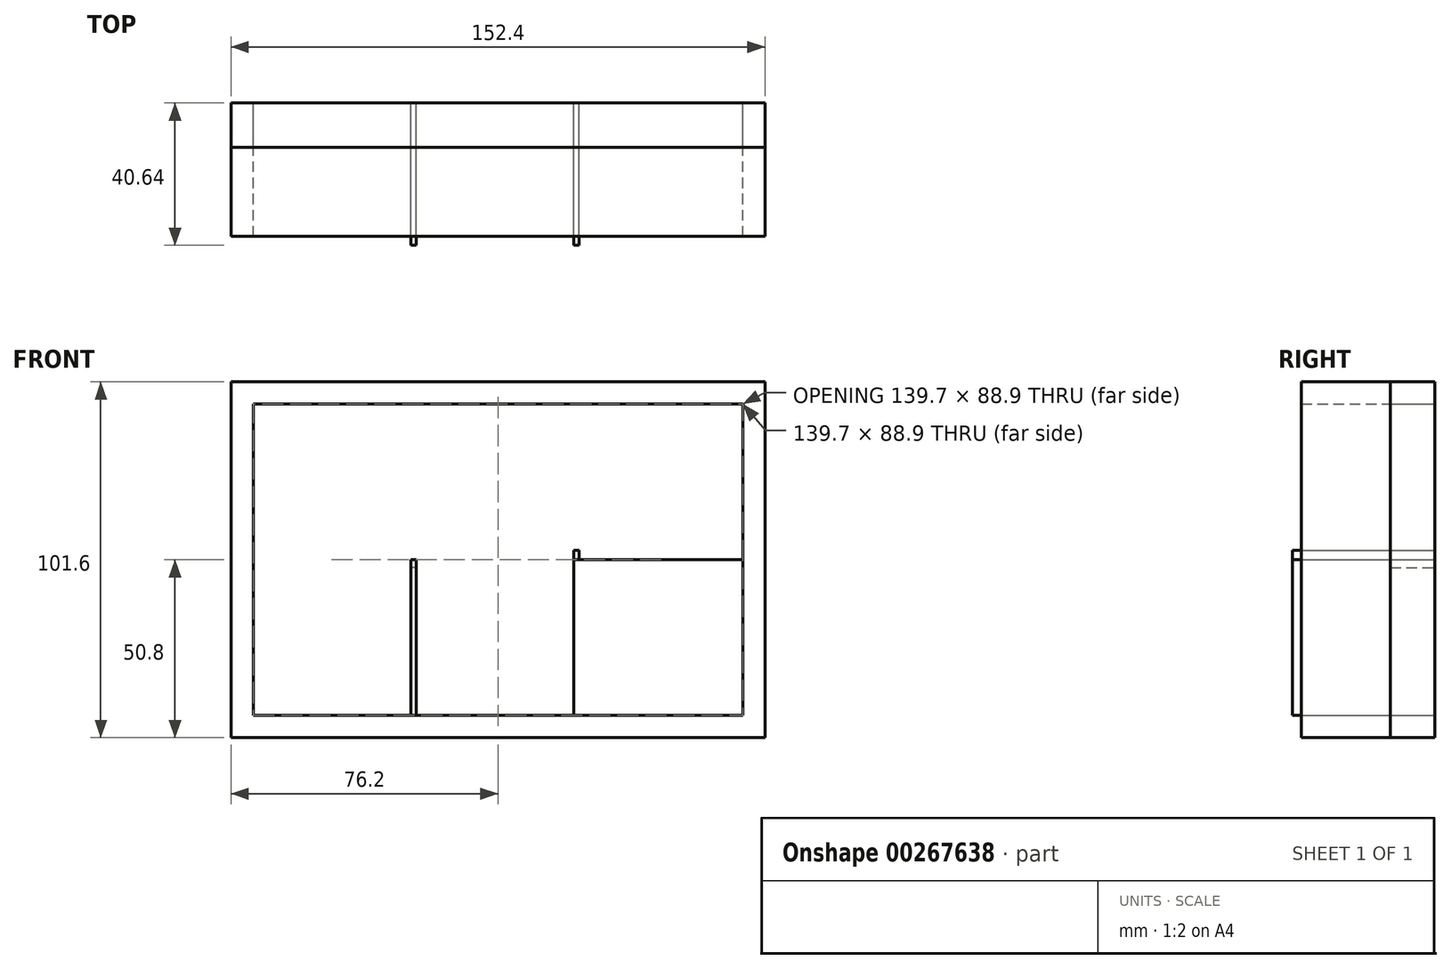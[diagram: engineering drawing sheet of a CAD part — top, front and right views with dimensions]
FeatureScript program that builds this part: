
annotation { "Feature Type Name" : "Feature", "Feature Type Description" : "" }
export const myFeature = defineFeature(function(context is Context, id is Id, definition is map)
    precondition{}
    {
        {
            var Q0;
            Q0=qCreatedBy(makeId("Front.planeOp"),FACE);
            var sketch = newSketch(context, id + "F0", { "sketchPlane" : qUnion([Q0])});
            skLineSegment(sketch, "E0.bottom", {"start": v(-76.2, 50.8) * mm, "end": v(76.2, 50.8) * mm});
            skLineSegment(sketch, "E0.top", {"start": v(-76.2, -50.8) * mm, "end": v(76.2, -50.8) * mm});
            skLineSegment(sketch, "E0.left", {"start": v(-76.2, 50.8) * mm, "end": v(-76.2, -50.8) * mm});
            skLineSegment(sketch, "E0.right", {"start": v(76.2, 50.8) * mm, "end": v(76.2, -50.8) * mm});
            skPoint(sketch, "E0.middle", {"position": v(0, 0) * mm});
            skLineSegment(sketch, "E1.bottom", {"start": v(69.85, 44.45) * mm, "end": v(-69.85, 44.45) * mm});
            skLineSegment(sketch, "E1.top", {"start": v(69.85, -44.45) * mm, "end": v(-69.85, -44.45) * mm});
            skLineSegment(sketch, "E1.left", {"start": v(69.85, 44.45) * mm, "end": v(69.85, -44.45) * mm});
            skLineSegment(sketch, "E1.right", {"start": v(-69.85, 44.45) * mm, "end": v(-69.85, -44.45) * mm});
            skLineSegment(sketch, "E2.bottom", {"start": v(-69.85, 44.45) * mm, "end": v(-23.37, 44.45) * mm});
            skLineSegment(sketch, "E2.top", {"start": v(-69.85, 0) * mm, "end": v(-23.37, 0) * mm});
            skLineSegment(sketch, "E2.left", {"start": v(-69.85, 44.45) * mm, "end": v(-69.85, 0) * mm});
            skLineSegment(sketch, "E2.right", {"start": v(-23.37, 44.45) * mm, "end": v(-23.37, 0) * mm});
            skLineSegment(sketch, "E3.bottom", {"start": v(-23.37, 44.45) * mm, "end": v(23.11, 44.45) * mm});
            skLineSegment(sketch, "E3.top", {"start": v(-23.37, 0) * mm, "end": v(23.11, 0) * mm});
            skLineSegment(sketch, "E3.right", {"start": v(23.11, 44.45) * mm, "end": v(23.11, 0) * mm});
            skLineSegment(sketch, "E4.bottom", {"start": v(23.11, 44.45) * mm, "end": v(69.85, 44.45) * mm});
            skLineSegment(sketch, "E4.top", {"start": v(23.11, 0) * mm, "end": v(69.85, 0) * mm});
            skLineSegment(sketch, "E4.right", {"start": v(69.85, 44.45) * mm, "end": v(69.85, 0) * mm});
            skLineSegment(sketch, "E5.top", {"start": v(23.11, -44.45) * mm, "end": v(69.85, -44.45) * mm});
            skLineSegment(sketch, "E5.left", {"start": v(23.11, 0) * mm, "end": v(23.11, -44.45) * mm});
            skLineSegment(sketch, "E5.right", {"start": v(69.85, 0) * mm, "end": v(69.85, -44.45) * mm});
            skLineSegment(sketch, "E6.top", {"start": v(-23.37, -44.45) * mm, "end": v(23.11, -44.45) * mm});
            skLineSegment(sketch, "E6.left", {"start": v(-23.37, 0) * mm, "end": v(-23.37, -44.45) * mm});
            skLineSegment(sketch, "E7.top", {"start": v(-69.85, -44.45) * mm, "end": v(-23.37, -44.45) * mm});
            skLineSegment(sketch, "E7.left", {"start": v(-69.85, 0) * mm, "end": v(-69.85, -44.45) * mm});
            skLineSegment(sketch, "E8.bottom", {"start": v(23.11, 44.45) * mm, "end": v(21.68, 44.45) * mm});
            skLineSegment(sketch, "E8.top", {"start": v(23.11, 0) * mm, "end": v(21.68, 0) * mm});
            skLineSegment(sketch, "E8.right", {"start": v(21.68, 44.45) * mm, "end": v(21.68, 0) * mm});
            skLineSegment(sketch, "E9.bottom", {"start": v(-23.37, 44.45) * mm, "end": v(-24.83, 44.45) * mm});
            skLineSegment(sketch, "E9.top", {"start": v(-23.37, -2.17) * mm, "end": v(-24.83, -2.17) * mm});
            skLineSegment(sketch, "E9.left", {"start": v(-23.37, 44.45) * mm, "end": v(-23.37, -2.17) * mm});
            skLineSegment(sketch, "E9.right", {"start": v(-24.83, 44.45) * mm, "end": v(-24.83, -2.17) * mm});
            skLineSegment(sketch, "E10.top", {"start": v(-23.37, -44.45) * mm, "end": v(-24.83, -44.45) * mm});
            skLineSegment(sketch, "E10.left", {"start": v(-23.37, -2.17) * mm, "end": v(-23.37, -44.45) * mm});
            skLineSegment(sketch, "E10.right", {"start": v(-24.83, -2.17) * mm, "end": v(-24.83, -44.45) * mm});
            skLineSegment(sketch, "E11.top", {"start": v(23.11, -44.45) * mm, "end": v(21.68, -44.45) * mm});
            skLineSegment(sketch, "E11.right", {"start": v(21.68, 0) * mm, "end": v(21.68, -44.45) * mm});
            skLineSegment(sketch, "E12.bottom", {"start": v(69.85, 0) * mm, "end": v(-69.85, 0) * mm});
            skLineSegment(sketch, "E12.top", {"start": v(69.85, 2.76) * mm, "end": v(-69.85, 2.76) * mm});
            skLineSegment(sketch, "E12.left", {"start": v(69.85, 0) * mm, "end": v(69.85, 2.76) * mm});
            skLineSegment(sketch, "E12.right", {"start": v(-69.85, 0) * mm, "end": v(-69.85, 2.76) * mm});
            skSolve(sketch);
        }
        {
            var Q0;
            Q0=makeQuery(id+"F0.imprint","IMPRINT",FACE,{"disambiguationData":[TD([[makeQuery(id+"F0.imprint","IMPRINT",EDGE,{"derivedFrom":sQuery(id+"F0.wireOp",EDGE,"E0.bottom")}),-1.0]])]});
            extrude(context, id + "F1", {"entities" : qUnion([Q0]), "depth" : 38.1 * mm});
        }
        {
            var Q0;
            Q0=makeQuery(id+"F0.imprint","IMPRINT",FACE,{"disambiguationData":[TD([[makeQuery(id+"F0.imprint","IMPRINT",EDGE,{"derivedFrom":sQuery(id+"F0.wireOp",EDGE,"E0.bottom")}),-1.0]])]});
            var Q1;
            Q1=makeQuery(id+"F0.imprint","IMPRINT",FACE,{"disambiguationData":[TD([[makeQuery(id+"F0.imprint","IMPRINT",EDGE,{"derivedFrom":sQuery(id+"F0.wireOp",EDGE,"E2.bottom")}),-1.0]])]});
            var Q2;
            Q2=makeQuery(id+"F0.imprint","IMPRINT",FACE,{"disambiguationData":[TD([[makeQuery(id+"F0.imprint","IMPRINT",EDGE,{"derivedFrom":sQuery(id+"F0.wireOp",EDGE,"E3.bottom")}),-1.0]])]});
            var Q3;
            Q3=makeQuery(id+"F0.imprint","IMPRINT",FACE,{"disambiguationData":[TD([[makeQuery(id+"F0.imprint","IMPRINT",EDGE,{"derivedFrom":sQuery(id+"F0.wireOp",EDGE,"E4.bottom")}),-1.0]])]});
            var Q4;
            Q4=makeQuery(id+"F0.imprint","IMPRINT",FACE,{"disambiguationData":[TD([[makeQuery(id+"F0.imprint","IMPRINT",EDGE,{"derivedFrom":sQuery(id+"F0.wireOp",EDGE,"E4.top")}),-1.0]])]});
            var Q5;
            Q5=makeQuery(id+"F0.imprint","IMPRINT",FACE,{"disambiguationData":[TD([[makeQuery(id+"F0.imprint","IMPRINT",EDGE,{"derivedFrom":sQuery(id+"F0.wireOp",EDGE,"E3.top")}),-1.0]])]});
            var Q6;
            Q6=makeQuery(id+"F0.imprint","IMPRINT",FACE,{"disambiguationData":[TD([[makeQuery(id+"F0.imprint","IMPRINT",EDGE,{"derivedFrom":sQuery(id+"F0.wireOp",EDGE,"E2.top")}),-1.0]])]});
            var Q7;
            Q7=makeQuery(id+"F0.imprint","IMPRINT",FACE,{"disambiguationData":[TD([[makeQuery(id+"F0.imprint","IMPRINT",EDGE,{"derivedFrom":sQuery(id+"F0.wireOp",EDGE,"E5.top")}),1.0]])]});
            var Q8;
            Q8=makeQuery(id+"F0.imprint","IMPRINT",FACE,{"disambiguationData":[TD([[makeQuery(id+"F0.imprint","IMPRINT",EDGE,{"derivedFrom":sQuery(id+"F0.wireOp",EDGE,"E6.top")}),1.0]])]});
            var Q9;
            Q9=makeQuery(id+"F0.imprint","IMPRINT",FACE,{"disambiguationData":[TD([[makeQuery(id+"F0.imprint","IMPRINT",EDGE,{"derivedFrom":sQuery(id+"F0.wireOp",EDGE,"E7.top")}),1.0]])]});
            extrude(context, id + "F2", {"entities" : qUnion([Q0, Q1, Q2, Q3, Q4, Q5, Q6, Q7, Q8, Q9]), "depth" : 12.7 * mm});
        }
        {
            var Q0;
            {var subQ0=sQuery(id+"F0.wireOp",EDGE,"E8.bottom");Q0=makeQuery(id+"F0.imprint","IMPRINT",FACE,{"disambiguationData":[TD([[makeQuery(id+"F0.imprint","IMPRINT",EDGE,{"derivedFrom":subQ0}),1.0]])]});}
            var Q1;
            {var subQ0=sQuery(id+"F0.wireOp",EDGE,"E9.bottom");Q1=makeQuery(id+"F0.imprint","IMPRINT",FACE,{"disambiguationData":[TD([[makeQuery(id+"F0.imprint","IMPRINT",EDGE,{"derivedFrom":subQ0}),1.0]])]});}
            var Q2;
            {var subQ3=sQuery(id+"F0.wireOp",EDGE,"E12.top");var subQ5=sQuery(id+"F0.wireOp",EDGE,"E9.left");var subQ6=makeQuery(id+"F0.imprint","INTERSECT",VERTEX,{"derivedFrom":[subQ5,subQ3]});Q2=makeQuery(id+"F0.imprint","IMPRINT",FACE,{"disambiguationData":[TD([[makeQuery(id+"F0.imprint","IMPRINT",EDGE,{"disambiguationData":[TD([[subQ6,-1.0]])],"derivedFrom":subQ5}),1.0]])]});}
            var Q3;
            {var subQ5=sQuery(id+"F0.wireOp",EDGE,"E12.left");Q3=makeQuery(id+"F0.imprint","IMPRINT",FACE,{"disambiguationData":[TD([[makeQuery(id+"F0.imprint","IMPRINT",EDGE,{"derivedFrom":subQ5}),1.0]])]});}
            var Q4;
            {var subQ1=sQuery(id+"F0.wireOp",EDGE,"E3.right");var subQ3=sQuery(id+"F0.wireOp",EDGE,"E12.top");var subQ4=makeQuery(id+"F0.imprint","INTERSECT",VERTEX,{"derivedFrom":[subQ1,subQ3]});Q4=makeQuery(id+"F0.imprint","IMPRINT",FACE,{"disambiguationData":[TD([[makeQuery(id+"F0.imprint","IMPRINT",EDGE,{"disambiguationData":[TD([[subQ4,-1.0]])],"derivedFrom":subQ3}),1.0]])]});}
            var Q5;
            Q5=makeQuery(id+"F0.imprint","IMPRINT",FACE,{"disambiguationData":[TD([[makeQuery(id+"F0.imprint","IMPRINT",EDGE,{"derivedFrom":sQuery(id+"F0.wireOp",EDGE,"E11.top")}),-1.0]])]});
            var Q6;
            Q6=makeQuery(id+"F0.imprint","IMPRINT",FACE,{"disambiguationData":[TD([[makeQuery(id+"F0.imprint","IMPRINT",EDGE,{"derivedFrom":sQuery(id+"F0.wireOp",EDGE,"E9.top")}),1.0]])]});
            var Q7;
            {var subQ0=sQuery(id+"F0.wireOp",EDGE,"E12.top");var subQ1=sQuery(id+"F0.wireOp",EDGE,"E9.left");var subQ2=makeQuery(id+"F0.imprint","INTERSECT",VERTEX,{"derivedFrom":[subQ1,subQ0]});Q7=makeQuery(id+"F0.imprint","IMPRINT",FACE,{"disambiguationData":[TD([[makeQuery(id+"F0.imprint","IMPRINT",EDGE,{"disambiguationData":[TD([[subQ2,-1.0]])],"derivedFrom":subQ1}),-1.0]])]});}
            var Q8;
            {var subQ0=sQuery(id+"F0.wireOp",EDGE,"E9.top");Q8=makeQuery(id+"F0.imprint","IMPRINT",FACE,{"disambiguationData":[TD([[makeQuery(id+"F0.imprint","IMPRINT",EDGE,{"derivedFrom":subQ0}),-1.0]])]});}
            var Q9;
            {var subQ5=sQuery(id+"F0.wireOp",EDGE,"E12.right");Q9=makeQuery(id+"F0.imprint","IMPRINT",FACE,{"disambiguationData":[TD([[makeQuery(id+"F0.imprint","IMPRINT",EDGE,{"derivedFrom":subQ5}),-1.0]])]});}
            extrude(context, id + "F3", {"entities" : qUnion([Q0, Q1, Q2, Q3, Q4, Q5, Q6, Q7, Q8, Q9]), "depth" : 40.64 * mm});
        }
    });
